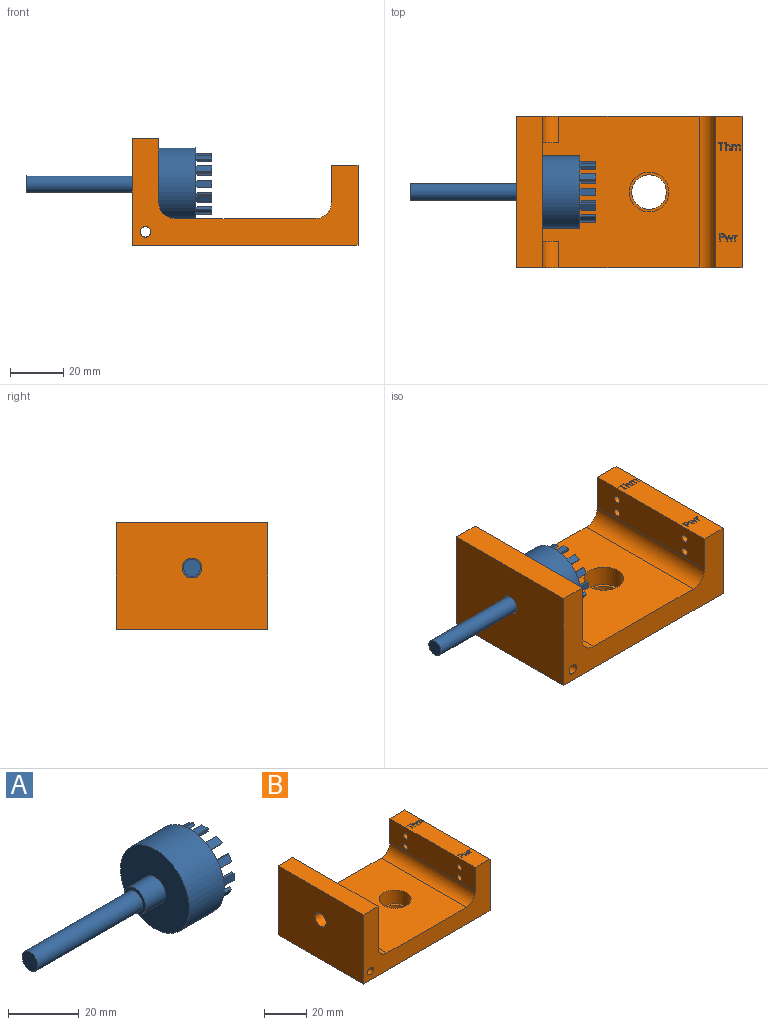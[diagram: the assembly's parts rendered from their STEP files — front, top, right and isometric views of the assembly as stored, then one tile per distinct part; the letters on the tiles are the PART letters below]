
ASSEMBLY  parts=2 mates=1
PART A: 87 faces, bbox 70x27.5x27.5 mm
  f0: plane 27.5x27.5mm, normal (1,0,0), area 555.6mm2, adj f1,f7,f8,f9,f10,f12,f13,f14
  f1: cylinder r=13.75mm len=27.5mm, axis (1,0,0), area 1209.5mm2, adj f0,f2
  f2: plane 27.5x27.5mm, normal (-1,0,0), area 537.2mm2, adj f1,f3
  f3: cylinder r=4.25mm len=8.5mm, axis (1,0,0), area 213.6mm2, adj f2,f4
  f4: plane 8.5x8.5mm, normal (-1,0,0), area 25.1mm2, adj f3,f5
  f5: cylinder r=3.17mm len=42mm, axis (1,0,0), area 837.9mm2, adj f4,f6
  f6: plane 6.35x6.35mm, normal (-1,0,0), area 31.7mm2, adj f5
  f7: plane 6x0.71mm, normal (0,0,-1), area 4.3mm2, adj f0,f8,f10,f11
  f8: cylinder r=4.25mm len=6mm, axis (-1,0,0), area 15.2mm2, adj f0,f7,f9,f11
  f9: plane 6x0.71mm, normal (0,0,1), area 4.3mm2, adj f0,f8,f10,f11
  f10: plane 6x2.5mm, normal (0,-1,0), area 15mm2, adj f0,f7,f9,f11
  f11: plane 2.5x0.9mm, normal (1,0,0), area 2.1mm2, adj f7,f8,f9,f10
  f12: cylinder r=4.25mm len=6mm, axis (-1,0,0), area 15.2mm2, adj f0,f13,f15,f16
  f13: plane 6x0.71mm, normal (0,-1,0), area 4.3mm2, adj f0,f12,f14,f16
  f14: plane 6x2.5mm, normal (0,0,-1), area 15mm2, adj f0,f13,f15,f16
  f15: plane 6x0.71mm, normal (0,1,0), area 4.3mm2, adj f0,f12,f14,f16
  f16: plane 2.5x0.9mm, normal (1,0,0), area 2.1mm2, adj f12,f13,f14,f15
  f17: cylinder r=4.25mm len=6mm, axis (-1,0,0), area 15.2mm2, adj f0,f18,f20,f21
  f18: plane 6x0.71mm, normal (0,0,-1), area 4.3mm2, adj f0,f17,f19,f21
  f19: plane 6x2.5mm, normal (0,1,0), area 15mm2, adj f0,f18,f20,f21
  f20: plane 6x0.71mm, normal (0,0,1), area 4.3mm2, adj f0,f17,f19,f21
  f21: plane 2.5x0.9mm, normal (1,0,0), area 2.1mm2, adj f17,f18,f19,f20
  f22: cylinder r=4.25mm len=6mm, axis (-1,0,0), area 15.2mm2, adj f0,f23,f25,f26
  f23: plane 6x0.71mm, normal (0,1,0), area 4.3mm2, adj f0,f22,f24,f26
  f24: plane 6x2.5mm, normal (0,0,1), area 15mm2, adj f0,f23,f25,f26
  f25: plane 6x0.71mm, normal (0,-1,0), area 4.3mm2, adj f0,f22,f24,f26
  f26: plane 2.5x0.9mm, normal (1,0,0), area 2.1mm2, adj f22,f23,f24,f25
  f27: plane 6x2.5mm, normal (0,0,1), area 15mm2, adj f0,f28,f30,f31
  f28: plane 6x1mm, normal (0,-1,0), area 6mm2, adj f0,f27,f29,f31
  f29: plane 6x2.5mm, normal (0,0,-1), area 15mm2, adj f0,f28,f30,f31
  f30: plane 6x1mm, normal (0,1,0), area 6mm2, adj f0,f27,f29,f31
  f31: plane 2.5x1mm, normal (1,0,0), area 2.5mm2, adj f27,f28,f29,f30
  f32: plane 6x0.87mm, normal (0,0.87,0.5), area 6mm2, adj f0,f33,f35,f36
  f33: plane 6x2.17mm, normal (0,-0.5,0.87), area 15mm2, adj f0,f32,f34,f36
  f34: plane 6x0.87mm, normal (0,-0.87,-0.5), area 6mm2, adj f0,f33,f35,f36
  f35: plane 6x2.17mm, normal (0,0.5,-0.87), area 15mm2, adj f0,f32,f34,f36
  f36: plane 2.67x2.12mm, normal (1,0,0), area 2.5mm2, adj f32,f33,f34,f35
  f37: plane 6x0.87mm, normal (0,0.5,0.87), area 6mm2, adj f0,f38,f40,f41
  f38: plane 6x2.17mm, normal (0,-0.87,0.5), area 15mm2, adj f0,f37,f39,f41
  f39: plane 6x0.87mm, normal (0,-0.5,-0.87), area 6mm2, adj f0,f38,f40,f41
  f40: plane 6x2.17mm, normal (0,0.87,-0.5), area 15mm2, adj f0,f37,f39,f41
  f41: plane 2.67x2.12mm, normal (1,0,0), area 2.5mm2, adj f37,f38,f39,f40
  f42: plane 6x1mm, normal (0,0,1), area 6mm2, adj f0,f43,f45,f46
  f43: plane 6x2.5mm, normal (0,-1,0), area 15mm2, adj f0,f42,f44,f46
  f44: plane 6x1mm, normal (0,0,-1), area 6mm2, adj f0,f43,f45,f46
  f45: plane 6x2.5mm, normal (0,1,0), area 15mm2, adj f0,f42,f44,f46
  f46: plane 2.5x1mm, normal (1,0,0), area 2.5mm2, adj f42,f43,f44,f45
  f47: plane 6x0.87mm, normal (0,-0.5,0.87), area 6mm2, adj f0,f48,f50,f51
  f48: plane 6x2.17mm, normal (0,-0.87,-0.5), area 15mm2, adj f0,f47,f49,f51
  f49: plane 6x0.87mm, normal (0,0.5,-0.87), area 6mm2, adj f0,f48,f50,f51
  f50: plane 6x2.17mm, normal (0,0.87,0.5), area 15mm2, adj f0,f47,f49,f51
  f51: plane 2.67x2.12mm, normal (1,0,0), area 2.5mm2, adj f47,f48,f49,f50
  f52: plane 6x0.87mm, normal (0,-0.87,0.5), area 6mm2, adj f0,f53,f55,f56
  f53: plane 6x2.17mm, normal (0,-0.5,-0.87), area 15mm2, adj f0,f52,f54,f56
  f54: plane 6x0.87mm, normal (0,0.87,-0.5), area 6mm2, adj f0,f53,f55,f56
  f55: plane 6x2.17mm, normal (0,0.5,0.87), area 15mm2, adj f0,f52,f54,f56
  f56: plane 2.67x2.12mm, normal (1,0,0), area 2.5mm2, adj f52,f53,f54,f55
  f57: plane 6x1mm, normal (0,-1,0), area 6mm2, adj f0,f58,f60,f61
  f58: plane 6x2.5mm, normal (0,0,-1), area 15mm2, adj f0,f57,f59,f61
  f59: plane 6x1mm, normal (0,1,0), area 6mm2, adj f0,f58,f60,f61
  f60: plane 6x2.5mm, normal (0,0,1), area 15mm2, adj f0,f57,f59,f61
  f61: plane 2.5x1mm, normal (1,0,0), area 2.5mm2, adj f57,f58,f59,f60
  f62: plane 6x0.87mm, normal (0,-0.87,-0.5), area 6mm2, adj f0,f63,f65,f66
  f63: plane 6x2.17mm, normal (0,0.5,-0.87), area 15mm2, adj f0,f62,f64,f66
  f64: plane 6x0.87mm, normal (0,0.87,0.5), area 6mm2, adj f0,f63,f65,f66
  f65: plane 6x2.17mm, normal (0,-0.5,0.87), area 15mm2, adj f0,f62,f64,f66
  f66: plane 2.67x2.12mm, normal (1,0,0), area 2.5mm2, adj f62,f63,f64,f65
  f67: plane 6x0.87mm, normal (0,-0.5,-0.87), area 6mm2, adj f0,f68,f70,f71
  f68: plane 6x2.17mm, normal (0,0.87,-0.5), area 15mm2, adj f0,f67,f69,f71
  f69: plane 6x0.87mm, normal (0,0.5,0.87), area 6mm2, adj f0,f68,f70,f71
  f70: plane 6x2.17mm, normal (0,-0.87,0.5), area 15mm2, adj f0,f67,f69,f71
  f71: plane 2.67x2.12mm, normal (1,0,0), area 2.5mm2, adj f67,f68,f69,f70
  f72: plane 6x1mm, normal (0,0,-1), area 6mm2, adj f0,f73,f75,f76
  f73: plane 6x2.5mm, normal (0,1,0), area 15mm2, adj f0,f72,f74,f76
  f74: plane 6x1mm, normal (0,0,1), area 6mm2, adj f0,f73,f75,f76
  f75: plane 6x2.5mm, normal (0,-1,0), area 15mm2, adj f0,f72,f74,f76
  f76: plane 2.5x1mm, normal (1,0,0), area 2.5mm2, adj f72,f73,f74,f75
  f77: plane 6x0.87mm, normal (0,0.5,-0.87), area 6mm2, adj f0,f78,f80,f81
  f78: plane 6x2.17mm, normal (0,0.87,0.5), area 15mm2, adj f0,f77,f79,f81
  f79: plane 6x0.87mm, normal (0,-0.5,0.87), area 6mm2, adj f0,f78,f80,f81
  f80: plane 6x2.17mm, normal (0,-0.87,-0.5), area 15mm2, adj f0,f77,f79,f81
  f81: plane 2.67x2.12mm, normal (1,0,0), area 2.5mm2, adj f77,f78,f79,f80
  f82: plane 6x0.87mm, normal (0,0.87,-0.5), area 6mm2, adj f0,f83,f85,f86
  f83: plane 6x2.17mm, normal (0,0.5,0.87), area 15mm2, adj f0,f82,f84,f86
  f84: plane 6x0.87mm, normal (0,-0.87,0.5), area 6mm2, adj f0,f83,f85,f86
  f85: plane 6x2.17mm, normal (0,-0.5,-0.87), area 15mm2, adj f0,f82,f84,f86
  f86: plane 2.67x2.12mm, normal (1,0,0), area 2.5mm2, adj f82,f83,f84,f85
PART B: 144 faces, bbox 85x57x40 mm
  f0: cylinder r=6mm len=10mm, axis (0,1,0), area 94.2mm2, adj f7,f9,f12,f142
  f1: plane 57x10mm, normal (0,0,1), area 556.2mm2, adj f2,f3,f11,f12,f29,f30,f31,f32
  f2: plane 57x30mm, normal (1,0,0), area 1646.8mm2, adj f1,f5,f11,f12,f17,f19,f21,f22
  f3: plane 57x14mm, normal (-1,0,0), area 769.7mm2, adj f1,f6,f11,f12,f21,f22,f23,f24
  f4: plane 57x40mm, normal (-1,0,0), area 2235.8mm2, adj f5,f10,f11,f12,f141
  f5: plane 85x57mm, normal (0,0,-1), area 4712.3mm2, adj f2,f4,f11,f12,f14
  f6: cylinder r=6mm len=57mm, axis (0,1,0), area 537.2mm2, adj f3,f7,f11,f12
  f7: plane 59x57mm, normal (0,0,1), area 3066.3mm2, adj f0,f6,f8,f9,f11,f12,f13,f142
  f8: cylinder r=6mm len=10mm, axis (0,1,0), area 94.2mm2, adj f7,f9,f11,f143
  f9: plane 57x30mm, normal (1,0,0), area 1545.8mm2, adj f0,f7,f8,f10,f11,f12,f141,f142
  f10: plane 57x10mm, normal (0,0,1), area 570mm2, adj f4,f9,f11,f12
  f11: plane 85x40mm, normal (0,-1,0), area 1352.9mm2, adj f1,f2,f3,f4,f5,f6,f7,f8
  f12: plane 85x40mm, normal (0,1,0), area 1352.9mm2, adj f0,f1,f2,f3,f4,f5,f6,f7
  f13: cylinder r=7.5mm len=15mm, axis (0,0,-1), area 377mm2, adj f7,f15
  f14: cylinder r=6.5mm len=13mm, axis (0,0,-1), area 81.7mm2, adj f5,f15
  f15: plane 15x15mm, normal (0,0,1), area 44mm2, adj f13,f14
  f16: cylinder r=2mm len=57mm, axis (0,1,0), area 716.3mm2, adj f11,f12
  f17: cylinder r=2mm len=6mm, axis (1,0,0), area 75.4mm2, adj f2,f18
  f18: plane 4x4mm, normal (1,0,0), area 12.6mm2, adj f17
  f19: cylinder r=2mm len=6mm, axis (1,0,0), area 75.4mm2, adj f2,f20
  f20: plane 4x4mm, normal (1,0,0), area 12.6mm2, adj f19
  f21: cylinder r=1.5mm len=10mm, axis (1,0,0), area 94.2mm2, adj f2,f3
  f22: cylinder r=1.5mm len=10mm, axis (1,0,0), area 94.2mm2, adj f2,f3
  f23: cylinder r=1.5mm len=10mm, axis (1,0,0), area 94.2mm2, adj f2,f3
  f24: cylinder r=1.5mm len=10mm, axis (1,0,0), area 94.2mm2, adj f2,f3
  f25: cone r=0mm half-angle=59deg, axis (1,0,0), area 5.7mm2, adj f26
  f26: cylinder r=1.25mm len=13.5mm, axis (1,0,0), area 106mm2, adj f2,f25
  f27: cone r=0mm half-angle=59deg, axis (1,0,0), area 5.7mm2, adj f28
  f28: cylinder r=1.25mm len=13.5mm, axis (1,0,0), area 106mm2, adj f2,f27
  f29: plane 1.31x0.5mm, normal (0.95,0.3,0), area 0.7mm2, adj f1,f30,f51,f52
  f30: plane 0.5x0.4mm, normal (0,1,0), area 0.2mm2, adj f1,f29,f31,f52
  f31: plane 2.23x0.62mm, normal (-0.96,0.27,0), area 1.2mm2, adj f1,f30,f32,f52
  f32: plane 0.5x0.35mm, normal (0,-1,0), area 0.2mm2, adj f1,f31,f33,f52
  f33: extruded ~1.64x0.5mm, area 0.8mm2, adj f1,f32,f34,f52
  f34: extruded ~0.5x0.23mm, area 0.1mm2, adj f1,f33,f35,f52
  f35: plane 0.5x0.02mm, normal (0,-1,0), area 0mm2, adj f1,f34,f36,f52
  f36: extruded ~0.59x0.5mm, area 0.3mm2, adj f1,f35,f37,f52
  f37: plane 1.28x0.5mm, normal (-0.95,-0.3,0), area 0.7mm2, adj f1,f36,f38,f52
  f38: plane 0.5x0.37mm, normal (0,-1,0), area 0.2mm2, adj f1,f37,f39,f52
  f39: plane 1.28x0.5mm, normal (0.95,-0.3,0), area 0.7mm2, adj f1,f38,f40,f52
  f40: extruded ~0.5x0.29mm, area 0.2mm2, adj f1,f39,f41,f52
  f41: extruded ~0.5x0.3mm, area 0.2mm2, adj f1,f40,f42,f52
  f42: plane 0.5x0.02mm, normal (0,-1,0), area 0mm2, adj f1,f41,f43,f52
  f43: extruded ~0.59x0.5mm, area 0.3mm2, adj f1,f42,f44,f52
  f44: extruded ~1.28x0.5mm, area 0.7mm2, adj f1,f43,f45,f52
  f45: plane 0.5x0.35mm, normal (0,-1,0), area 0.2mm2, adj f1,f44,f46,f52
  f46: plane 2.23x0.61mm, normal (0.96,0.26,0), area 1.2mm2, adj f1,f45,f47,f52
  f47: plane 0.5x0.39mm, normal (0,1,0), area 0.2mm2, adj f1,f46,f48,f52
  f48: plane 1.3x0.5mm, normal (-0.95,0.31,0), area 0.7mm2, adj f1,f47,f49,f52
  f49: extruded ~0.55x0.5mm, area 0.3mm2, adj f1,f48,f50,f52
  f50: plane 0.5x0.02mm, normal (0,1,0), area 0mm2, adj f1,f49,f51,f52
  f51: extruded ~0.55x0.5mm, area 0.3mm2, adj f1,f29,f50,f52
  f52: plane 3.15x2.23mm, normal (0,0,1), area 2.7mm2, adj f29,f30,f31,f32,f33,f34,f35,f36
  f53: plane 0.5x0.31mm, normal (0,-1,0), area 0.2mm2, adj f54,f67,f68,f140
  f54: plane 1.21x0.5mm, normal (-1,0,0), area 0.6mm2, adj f53,f55,f68,f140
  f55: plane 0.5x0.39mm, normal (0,1,0), area 0.2mm2, adj f54,f56,f68,f140
  f56: extruded ~0.6x0.5mm, area 0.3mm2, adj f55,f57,f68,f140
  f57: extruded ~0.5x0.44mm, area 0.2mm2, adj f56,f58,f68,f140
  f58: extruded ~0.5x0.48mm, area 0.3mm2, adj f57,f67,f68,f140
  f59: extruded ~0.7x0.5mm, area 0.4mm2, adj f1,f60,f66,f68
  f60: extruded ~1.11x0.87mm, area 0.8mm2, adj f1,f59,f61,f68
  f61: plane 0.77x0.5mm, normal (0,-1,0), area 0.4mm2, adj f1,f60,f62,f68
  f62: plane 2.97x0.5mm, normal (1,0,0), area 1.5mm2, adj f1,f61,f63,f68
  f63: plane 0.5x0.35mm, normal (0,1,0), area 0.2mm2, adj f1,f62,f64,f68
  f64: plane 1.17x0.5mm, normal (-1,0,0), area 0.6mm2, adj f1,f63,f65,f68
  f65: plane 0.5x0.35mm, normal (0,1,0), area 0.2mm2, adj f1,f64,f66,f68
  f66: extruded ~0.88x0.5mm, area 0.5mm2, adj f1,f59,f65,f68
  f67: extruded ~0.67x0.5mm, area 0.3mm2, adj f53,f58,f68,f140
  f68: plane 2.97x1.89mm, normal (0,0,1), area 2.2mm2, adj f53,f54,f55,f56,f57,f58,f59,f60
  f69: extruded ~0.5x0.27mm, area 0.1mm2, adj f1,f70,f81,f82
  f70: extruded ~0.5x0.38mm, area 0.2mm2, adj f1,f69,f71,f82
  f71: extruded ~0.5x0.34mm, area 0.2mm2, adj f1,f70,f72,f82
  f72: plane 0.5x0.02mm, normal (0,-1,0), area 0mm2, adj f1,f71,f73,f82
  f73: plane 0.5x0.41mm, normal (-1,-0.09,0), area 0.2mm2, adj f1,f72,f74,f82
  f74: plane 0.5x0.28mm, normal (0,-1,0), area 0.1mm2, adj f1,f73,f75,f82
  f75: plane 2.23x0.5mm, normal (1,0,0), area 1.1mm2, adj f1,f74,f76,f82
  f76: plane 0.5x0.34mm, normal (0,1,0), area 0.2mm2, adj f1,f75,f77,f82
  f77: plane 1.2x0.5mm, normal (-1,0,0), area 0.6mm2, adj f1,f76,f78,f82
  f78: extruded ~0.55x0.5mm, area 0.3mm2, adj f1,f77,f79,f82
  f79: extruded ~0.5x0.46mm, area 0.3mm2, adj f1,f78,f80,f82
  f80: extruded ~0.5x0.24mm, area 0.1mm2, adj f1,f79,f81,f82
  f81: plane 0.5x0.31mm, normal (-0.99,0.15,0), area 0.2mm2, adj f1,f69,f80,f82
  f82: plane 2.27x1.28mm, normal (0,0,1), area 1mm2, adj f69,f70,f71,f72,f73,f74,f75,f76
  f83: plane 0.5x0.35mm, normal (0,1,0), area 0.2mm2, adj f1,f84,f90,f91
  f84: plane 2.67x0.5mm, normal (-1,0,0), area 1.3mm2, adj f1,f83,f85,f91
  f85: plane 0.94x0.5mm, normal (0,1,0), area 0.5mm2, adj f1,f84,f86,f91
  f86: plane 0.5x0.31mm, normal (-1,0,0), area 0.2mm2, adj f1,f85,f87,f91
  f87: plane 2.23x0.5mm, normal (0,-1,0), area 1.1mm2, adj f1,f86,f88,f91
  f88: plane 0.5x0.31mm, normal (1,0,0), area 0.2mm2, adj f1,f87,f89,f91
  f89: plane 0.94x0.5mm, normal (0,1,0), area 0.5mm2, adj f1,f88,f90,f91
  f90: plane 2.67x0.5mm, normal (1,0,0), area 1.3mm2, adj f1,f83,f89,f91
  f91: plane 2.97x2.23mm, normal (0,0,1), area 1.6mm2, adj f83,f84,f85,f86,f87,f88,f89,f90
  f92: plane 1.44x0.5mm, normal (1,0,0), area 0.7mm2, adj f1,f93,f109,f110
  f93: plane 0.5x0.34mm, normal (0,1,0), area 0.2mm2, adj f1,f92,f94,f110
  f94: plane 1.45x0.5mm, normal (-1,0,0), area 0.7mm2, adj f1,f93,f95,f110
  f95: extruded ~0.62x0.5mm, area 0.3mm2, adj f1,f94,f96,f110
  f96: extruded ~0.61x0.5mm, area 0.3mm2, adj f1,f95,f97,f110
  f97: extruded ~0.5x0.42mm, area 0.2mm2, adj f1,f96,f98,f110
  f98: extruded ~0.5x0.28mm, area 0.2mm2, adj f1,f97,f99,f110
  f99: plane 0.5x0.02mm, normal (0,-1,0), area 0mm2, adj f1,f98,f100,f110
  f100: extruded ~0.5x0.29mm, area 0.1mm2, adj f1,f99,f101,f110
  f101: plane 0.96x0.5mm, normal (-1,0,0), area 0.5mm2, adj f1,f100,f102,f110
  f102: plane 0.5x0.34mm, normal (0,-1,0), area 0.2mm2, adj f1,f101,f103,f110
  f103: plane 3.17x0.5mm, normal (1,0,0), area 1.6mm2, adj f1,f102,f104,f110
  f104: plane 0.5x0.34mm, normal (0,1,0), area 0.2mm2, adj f1,f103,f105,f110
  f105: plane 1.17x0.5mm, normal (-1,0,0), area 0.6mm2, adj f1,f104,f106,f110
  f106: extruded ~0.63x0.5mm, area 0.3mm2, adj f1,f105,f107,f110
  f107: extruded ~0.51x0.5mm, area 0.3mm2, adj f1,f106,f108,f110
  f108: extruded ~0.5x0.39mm, area 0.2mm2, adj f1,f107,f109,f110
  f109: extruded ~0.5x0.41mm, area 0.2mm2, adj f1,f92,f108,f110
  f110: plane 3.17x1.86mm, normal (0,0,1), area 2.1mm2, adj f92,f93,f94,f95,f96,f97,f98,f99
  f111: plane 1.45x0.5mm, normal (1,0,0), area 0.7mm2, adj f1,f112,f138,f139
  f112: plane 0.5x0.34mm, normal (0,1,0), area 0.2mm2, adj f1,f111,f113,f139
  f113: plane 1.45x0.5mm, normal (-1,0,0), area 0.7mm2, adj f1,f112,f114,f139
  f114: extruded ~0.62x0.5mm, area 0.3mm2, adj f1,f113,f115,f139
  f115: extruded ~0.57x0.5mm, area 0.3mm2, adj f1,f114,f116,f139
  f116: extruded ~0.5x0.43mm, area 0.2mm2, adj f1,f115,f117,f139
  f117: extruded ~0.5x0.29mm, area 0.2mm2, adj f1,f116,f118,f139
  f118: plane 0.5x0.02mm, normal (0,-1,0), area 0mm2, adj f1,f117,f119,f139
  f119: extruded ~0.68x0.5mm, area 0.4mm2, adj f1,f118,f120,f139
  f120: extruded ~0.5x0.39mm, area 0.2mm2, adj f1,f119,f121,f139
  f121: extruded ~0.5x0.27mm, area 0.2mm2, adj f1,f120,f122,f139
  f122: plane 0.5x0.02mm, normal (0,-1,0), area 0mm2, adj f1,f121,f123,f139
  f123: plane 0.5x0.31mm, normal (-0.98,-0.18,0), area 0.2mm2, adj f1,f122,f124,f139
  f124: plane 0.5x0.27mm, normal (0,-1,0), area 0.1mm2, adj f1,f123,f125,f139
  f125: plane 2.23x0.5mm, normal (1,0,0), area 1.1mm2, adj f1,f124,f126,f139
  f126: plane 0.5x0.34mm, normal (0,1,0), area 0.2mm2, adj f1,f125,f127,f139
  f127: plane 1.17x0.5mm, normal (-1,0,0), area 0.6mm2, adj f1,f126,f128,f139
  f128: extruded ~0.62x0.5mm, area 0.3mm2, adj f1,f127,f129,f139
  f129: extruded ~0.5x0.46mm, area 0.3mm2, adj f1,f128,f130,f139
  f130: extruded ~0.5x0.36mm, area 0.2mm2, adj f1,f129,f131,f139
  f131: extruded ~0.5x0.4mm, area 0.2mm2, adj f1,f130,f132,f139
  f132: plane 1.45x0.5mm, normal (1,0,0), area 0.7mm2, adj f1,f131,f133,f139
  f133: plane 0.5x0.34mm, normal (0,1,0), area 0.2mm2, adj f1,f132,f134,f139
  f134: plane 1.25x0.5mm, normal (-1,0,0), area 0.6mm2, adj f1,f133,f135,f139
  f135: extruded ~0.56x0.5mm, area 0.3mm2, adj f1,f134,f136,f139
  f136: extruded ~0.5x0.47mm, area 0.3mm2, adj f1,f135,f137,f139
  f137: extruded ~0.5x0.35mm, area 0.2mm2, adj f1,f136,f138,f139
  f138: extruded ~0.5x0.4mm, area 0.2mm2, adj f1,f111,f137,f139
  f139: plane 3.18x2.27mm, normal (0,0,1), area 2.8mm2, adj f111,f112,f113,f114,f115,f116,f117,f118
  f140: plane 1.21x1.18mm, normal (0,0,1), area 1.3mm2, adj f53,f54,f55,f56,f57,f58,f67
  f141: cylinder r=3.75mm len=10mm, axis (-1,0,0), area 235.6mm2, adj f4,f9
  f142: plane 6x6mm, normal (0,-1,0), area 7.7mm2, adj f0,f7,f9
  f143: plane 6x6mm, normal (0,1,0), area 7.7mm2, adj f7,f8,f9
PLACE A t=(-16.15,9.07,46.65)mm
PLACE B t=(44.85,9.07,23.65)mm
MATE fastened B.f141 <-> A.f1  axis (-1,0,0) through (-30.15,9.07,46.65)mm
